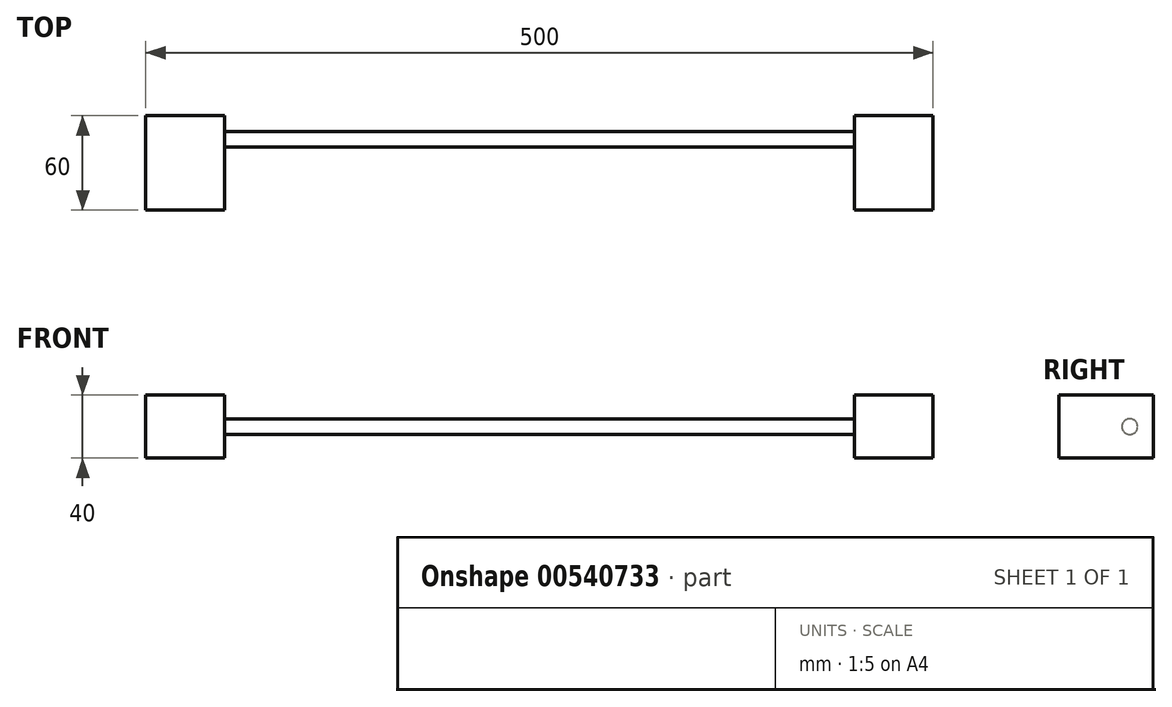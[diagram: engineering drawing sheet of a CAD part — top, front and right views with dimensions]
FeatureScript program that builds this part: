
annotation { "Feature Type Name" : "Feature", "Feature Type Description" : "" }
export const myFeature = defineFeature(function(context is Context, id is Id, definition is map)
    precondition{}
    {
        {
            var Q0;
            Q0=qCreatedBy(makeId("Top.planeOp"),FACE);
            var sketch = newSketch(context, id + "F0", { "sketchPlane" : qUnion([Q0])});
            skLineSegment(sketch, "E0", {"start": v(-175.64, -60) * mm, "end": v(229.54, -60) * mm, "construction": true});
            skLineSegment(sketch, "E1.bottom", {"start": v(-150, -60) * mm, "end": v(-100, -60) * mm});
            skLineSegment(sketch, "E1.top", {"start": v(-150, 0) * mm, "end": v(-100, 0) * mm});
            skLineSegment(sketch, "E1.left", {"start": v(-150, -60) * mm, "end": v(-150, 0) * mm});
            skLineSegment(sketch, "E1.right", {"start": v(-100, -60) * mm, "end": v(-100, 0) * mm});
            skLineSegment(sketch, "E2", {"start": v(-100, 0) * mm, "end": v(208.6, 0) * mm, "construction": true});
            skLineSegment(sketch, "E3.bottom", {"start": v(350, 0) * mm, "end": v(300, 0) * mm});
            skLineSegment(sketch, "E3.top", {"start": v(350, -60) * mm, "end": v(300, -60) * mm});
            skLineSegment(sketch, "E3.left", {"start": v(350, 0) * mm, "end": v(350, -60) * mm});
            skLineSegment(sketch, "E3.right", {"start": v(300, 0) * mm, "end": v(300, -60) * mm});
            skSolve(sketch);
        }
        {
            var Q0;
            Q0=makeQuery(id+"F0.imprint","IMPRINT",FACE,{"disambiguationData":[TD([[makeQuery(id+"F0.imprint","IMPRINT",EDGE,{"derivedFrom":sQuery(id+"F0.wireOp",EDGE,"E1.bottom")}),1.0]])]});
            var Q1;
            Q1=makeQuery(id+"F0.imprint","IMPRINT",FACE,{"disambiguationData":[TD([[makeQuery(id+"F0.imprint","IMPRINT",EDGE,{"derivedFrom":sQuery(id+"F0.wireOp",EDGE,"E3.bottom")}),1.0]])]});
            extrude(context, id + "F1", {"entities" : qUnion([Q0, Q1]), "depth" : 40 * mm, "offsetDistance" : 25 * mm});
        }
        {
            var Q0;
            Q0=makeQuery(id+"F1.opExtrude","SWEPT_FACE",FACE,{"disambiguationData":[OSD([sQuery(id+"F0.wireOp",EDGE,"E3.left")])]});
            var sketch = newSketch(context, id + "F2", { "sketchPlane" : qUnion([Q0])});
            skCircle(sketch, "E4", {"center": v(-15, 20) * mm, "radius": 5 * mm});
            skPoint(sketch, "E4.centerSnap0", {"position": v(-30, 40) * mm});
            skSolve(sketch);
        }
        {
            var Q0;
            Q0 = qSketchRegion(id + "F2", true);
            var Q1;
            Q1=makeQuery(id+"F1.opExtrude","SWEPT_FACE",FACE,{"disambiguationData":[OSD([sQuery(id+"F0.wireOp",EDGE,"E1.right")])]});
            var Q2;
            Q2=makeQuery(id+"F1.opExtrude","SWEPT_FACE",FACE,{"disambiguationData":[OSD([sQuery(id+"F0.wireOp",EDGE,"E3.right")])]});
            extrude(context, id + "F3", {"entities" : qUnion([Q0]), "endBound" : BoundingType.UP_TO_SURFACE, "oppositeDirection" : true, "depth" : 321.9 * mm, "endBoundEntityFace" : qUnion([Q1]), "offsetDistance" : 25 * mm, "hasSecondDirection" : true, "secondDirectionBound" : SecondDirectionBoundingType.UP_TO_SURFACE, "secondDirectionOppositeDirection" : true, "secondDirectionDepth" : 25 * mm, "secondDirectionBoundEntityFace" : qUnion([Q2])});
        }
    });
